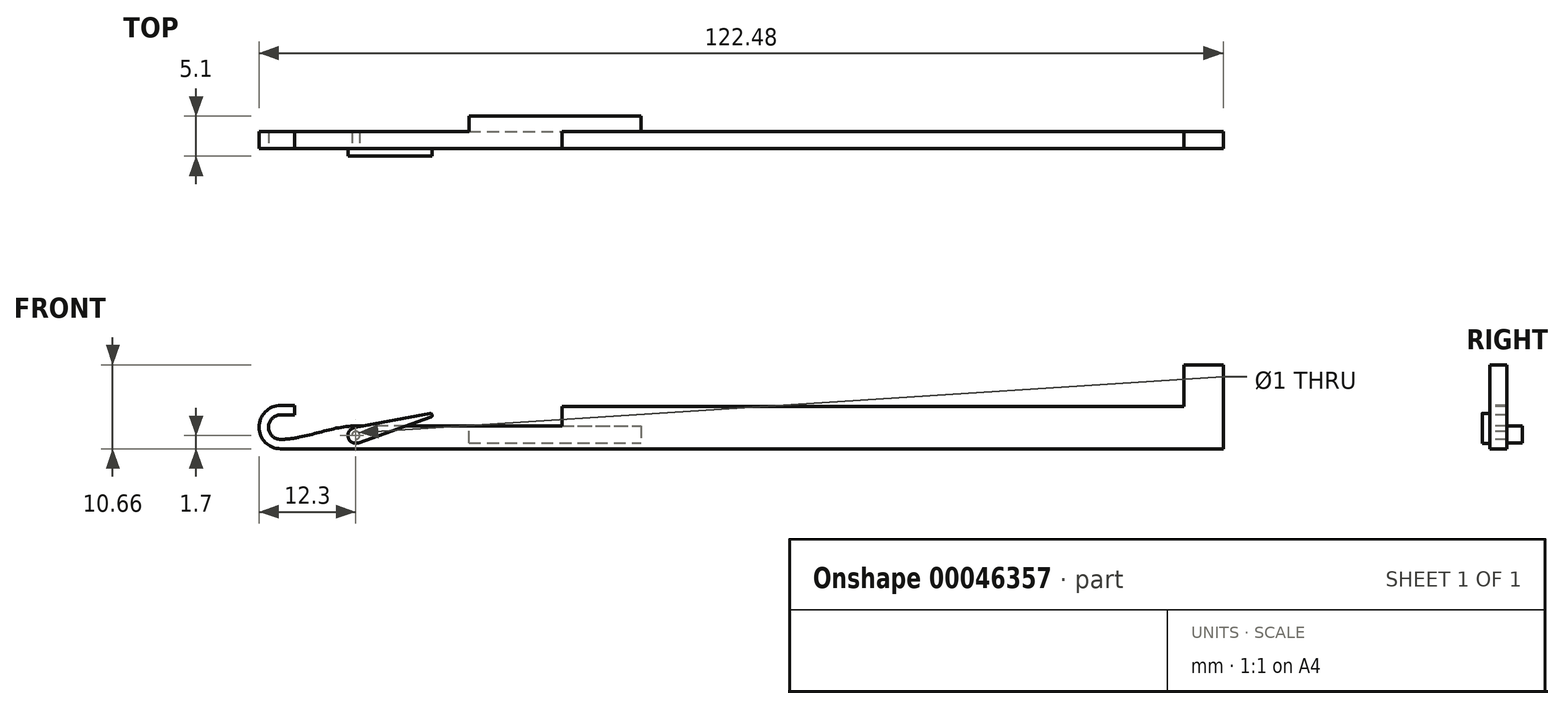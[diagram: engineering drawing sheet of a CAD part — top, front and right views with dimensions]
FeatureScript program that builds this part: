
annotation { "Feature Type Name" : "Feature", "Feature Type Description" : "" }
export const myFeature = defineFeature(function(context is Context, id is Id, definition is map)
    precondition{}
    {
        {
            var Q0;
            Q0=qCreatedBy(makeId("Front.planeOp"),FACE);
            var sketch = newSketch(context, id + "F0", { "sketchPlane" : qUnion([Q0])});
            skLineSegment(sketch, "E0.bottom", {"start": v(-122.48, 10.66) * mm, "end": v(-4.98, 10.66) * mm});
            skLineSegment(sketch, "E0.top", {"start": v(-122.48, 0) * mm, "end": v(0, 0) * mm});
            skLineSegment(sketch, "E0.left", {"start": v(-122.48, 10.66) * mm, "end": v(-122.48, 0) * mm});
            skLineSegment(sketch, "E0.right", {"start": v(0, 10.66) * mm, "end": v(0, 0) * mm});
            skLineSegment(sketch, "E1", {"start": v(-4.98, 10.66) * mm, "end": v(0, 10.66) * mm});
            skLineSegment(sketch, "E2", {"start": v(-4.98, 5.36) * mm, "end": v(-83.98, 5.36) * mm});
            skLineSegment(sketch, "E3", {"start": v(-83.98, 5.36) * mm, "end": v(-83.98, 2.9) * mm});
            skLineSegment(sketch, "E4", {"start": v(-83.98, 2.9) * mm, "end": v(-110.18, 2.9) * mm});
            skCircle(sketch, "E5", {"center": v(-119.73, 2.75) * mm, "radius": 2.75 * mm});
            skCircle(sketch, "E6.0", {"center": v(-119.73, 2.75) * mm, "radius": 1.55 * mm});
            skLineSegment(sketch, "E7", {"start": v(-117.98, 10.66) * mm, "end": v(-117.98, 0) * mm, "construction": true});
            skLineSegment(sketch, "E8", {"start": v(-4.98, 10.66) * mm, "end": v(-4.98, 5.36) * mm});
            skLineSegment(sketch, "E9", {"start": v(-100.48, 10.66) * mm, "end": v(-100.48, 0) * mm, "construction": true});
            skLineSegment(sketch, "E10", {"start": v(-119.73, 5.5) * mm, "end": v(-117.98, 5.5) * mm});
            skLineSegment(sketch, "E11", {"start": v(-119.73, 4.3) * mm, "end": v(-117.98, 4.3) * mm});
            skLineSegment(sketch, "E12", {"start": v(-117.98, 5.5) * mm, "end": v(-117.98, 4.3) * mm});
            skLineSegment(sketch, "E13", {"start": v(-119.73, 1.2) * mm, "end": v(-59.18, 1.2) * mm, "construction": true});
            skFitSpline(sketch, "E14", {"points": [v(-119.73, 1.2) * mm, v(-110.18, 2.9) * mm], "startDerivative": vector(9.67, 0) * mm, "endDerivative": vector(9.68, 0) * mm});
            skCircle(sketch, "E15", {"center": v(-110.18, 1.7) * mm, "radius": 0.5 * mm});
            skLineSegment(sketch, "E16", {"start": v(-95.81, 0.75) * mm, "end": v(-73.98, 0.75) * mm});
            skLineSegment(sketch, "E17", {"start": v(-95.81, 0.75) * mm, "end": v(-95.81, 2.9) * mm});
            skLineSegment(sketch, "E18", {"start": v(-95.81, 2.9) * mm, "end": v(-73.98, 2.9) * mm});
            skLineSegment(sketch, "E19", {"start": v(-73.98, 2.9) * mm, "end": v(-73.98, 0.75) * mm});
            skPoint(sketch, "E20", {"position": v(-100.48, 4.5) * mm});
            skCircle(sketch, "E21", {"center": v(-110.18, 1.7) * mm, "radius": 1 * mm});
            skCircle(sketch, "E22", {"center": v(-100.73, 4.25) * mm, "radius": 0.25 * mm});
            skLineSegment(sketch, "E23", {"start": v(-49.44, 4.5) * mm, "end": v(-100.48, 4.5) * mm, "construction": true});
            skLineSegment(sketch, "E24", {"start": v(-109.85, 0.76) * mm, "end": v(-100.65, 4.01) * mm});
            skLineSegment(sketch, "E25", {"start": v(-110.37, 2.68) * mm, "end": v(-100.78, 4.5) * mm});
            skSolve(sketch);
        }
        {
            var Q0;
            {var subQ6=sQuery(id+"F0.wireOp",EDGE,"E0.right");Q0=makeQuery(id+"F0.imprint","IMPRINT",FACE,{"disambiguationData":[TD([[makeQuery(id+"F0.imprint","IMPRINT",EDGE,{"derivedFrom":subQ6}),-1.0]])]});}
            var Q1;
            {var subQ3=sQuery(id+"F0.wireOp",EDGE,"E11");Q1=makeQuery(id+"F0.imprint","IMPRINT",FACE,{"disambiguationData":[TD([[makeQuery(id+"F0.imprint","IMPRINT",EDGE,{"derivedFrom":subQ3}),1.0]])]});}
            var Q2;
            {var subQ3=sQuery(id+"F0.wireOp",EDGE,"E10");Q2=makeQuery(id+"F0.imprint","IMPRINT",FACE,{"disambiguationData":[TD([[makeQuery(id+"F0.imprint","IMPRINT",EDGE,{"derivedFrom":subQ3}),-1.0]])]});}
            var Q3;
            {var subQ1=sQuery(id+"F0.wireOp",EDGE,"E4");var subQ5=sQuery(id+"F0.wireOp",EDGE,"E24");var subQ6=makeQuery(id+"F0.imprint","INTERSECT",VERTEX,{"derivedFrom":[subQ1,subQ5]});Q3=makeQuery(id+"F0.imprint","IMPRINT",FACE,{"disambiguationData":[TD([[makeQuery(id+"F0.imprint","IMPRINT",EDGE,{"disambiguationData":[TD([[subQ6,-1.0]])],"derivedFrom":subQ1}),1.0]])]});}
            var Q4;
            Q4=makeQuery(id+"F0.imprint","IMPRINT",FACE,{"disambiguationData":[TD([[makeQuery(id+"F0.imprint","IMPRINT",EDGE,{"derivedFrom":sQuery(id+"F0.wireOp",EDGE,"E15")}),-1.0]])]});
            extrude(context, id + "F1", {"entities" : qUnion([Q0, Q1, Q2, Q3, Q4]), "oppositeDirection" : true, "depth" : 2.15 * mm});
        }
        {
            var Q0;
            Q0=makeQuery(id+"F0.imprint","IMPRINT",FACE,{"disambiguationData":[TD([[makeQuery(id+"F0.imprint","IMPRINT",EDGE,{"derivedFrom":sQuery(id+"F0.wireOp",EDGE,"E16")}),1.0]])]});
            extrude(context, id + "F2", {"entities" : qUnion([Q0]), "operationType" : NewBodyOperationType.ADD, "oppositeDirection" : true, "depth" : 4.1 * mm});
        }
        {
            var Q0;
            Q0=makeQuery(id+"F0.imprint","IMPRINT",FACE,{"disambiguationData":[TD([[makeQuery(id+"F0.imprint","IMPRINT",EDGE,{"derivedFrom":sQuery(id+"F0.wireOp",EDGE,"E15")}),-1.0]])]});
            var Q1;
            {var subQ1=sQuery(id+"F0.wireOp",EDGE,"E4");var subQ5=sQuery(id+"F0.wireOp",EDGE,"E24");var subQ6=makeQuery(id+"F0.imprint","INTERSECT",VERTEX,{"derivedFrom":[subQ1,subQ5]});Q1=makeQuery(id+"F0.imprint","IMPRINT",FACE,{"disambiguationData":[TD([[makeQuery(id+"F0.imprint","IMPRINT",EDGE,{"disambiguationData":[TD([[subQ6,-1.0]])],"derivedFrom":subQ1}),1.0]])]});}
            var Q2;
            {var subQ1=sQuery(id+"F0.wireOp",EDGE,"E4");var subQ5=sQuery(id+"F0.wireOp",EDGE,"E24");var subQ6=makeQuery(id+"F0.imprint","INTERSECT",VERTEX,{"derivedFrom":[subQ1,subQ5]});Q2=makeQuery(id+"F0.imprint","IMPRINT",FACE,{"disambiguationData":[TD([[makeQuery(id+"F0.imprint","IMPRINT",EDGE,{"disambiguationData":[TD([[subQ6,-1.0]])],"derivedFrom":subQ1}),-1.0]])]});}
            var Q3;
            {var subQ0=sQuery(id+"F0.wireOp",EDGE,"E22");var subQ2=makeQuery(id+"F0.imprint","INTERSECT",VERTEX,{"derivedFrom":[subQ0,sQuery(id+"F0.wireOp",EDGE,"E24")]});Q3=makeQuery(id+"F0.imprint","IMPRINT",FACE,{"disambiguationData":[TD([[makeQuery(id+"F0.imprint","IMPRINT",EDGE,{"disambiguationData":[TD([[subQ2,1.0]])],"derivedFrom":subQ0}),1.0]])]});}
            var Q4;
            Q4=makeQuery(id+"F0.imprint","IMPRINT",FACE,{"disambiguationData":[TD([[makeQuery(id+"F0.imprint","IMPRINT",EDGE,{"derivedFrom":sQuery(id+"F0.wireOp",EDGE,"E15")}),1.0]])]});
            extrude(context, id + "F3", {"entities" : qUnion([Q0, Q1, Q2, Q3, Q4]), "depth" : 1 * mm});
        }
    });
